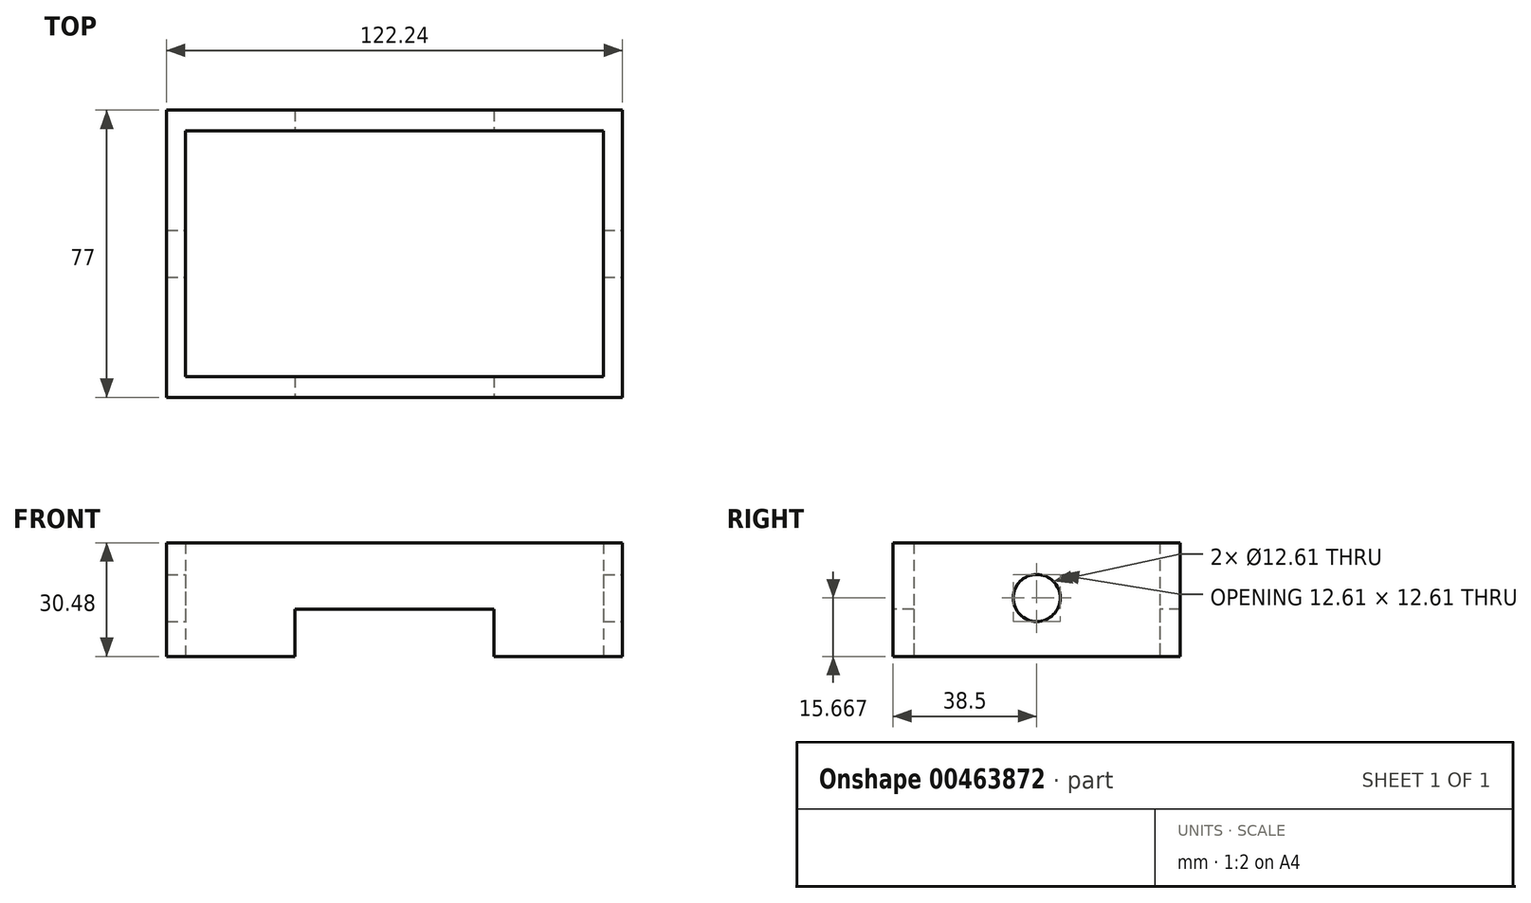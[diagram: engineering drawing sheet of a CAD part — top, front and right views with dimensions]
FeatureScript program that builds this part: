
annotation { "Feature Type Name" : "Feature", "Feature Type Description" : "" }
export const myFeature = defineFeature(function(context is Context, id is Id, definition is map)
    precondition{}
    {
        {
            var Q0;
            Q0=qCreatedBy(makeId("Top.planeOp"),FACE);
            var sketch = newSketch(context, id + "F0", { "sketchPlane" : qUnion([Q0])});
            skLineSegment(sketch, "E0.bottom", {"start": v(-61.12, 38.5) * mm, "end": v(61.12, 38.5) * mm});
            skLineSegment(sketch, "E0.top", {"start": v(-61.12, -38.5) * mm, "end": v(61.12, -38.5) * mm});
            skLineSegment(sketch, "E0.left", {"start": v(-61.12, 38.5) * mm, "end": v(-61.12, -38.5) * mm});
            skLineSegment(sketch, "E0.right", {"start": v(61.12, 38.5) * mm, "end": v(61.12, -38.5) * mm});
            skPoint(sketch, "E0.middle", {"position": v(0, 0) * mm});
            skSolve(sketch);
        }
        {
            var Q0;
            Q0=makeQuery(id+"F0.imprint","IMPRINT",FACE,{"disambiguationData":[TD([[makeQuery(id+"F0.imprint","IMPRINT",EDGE,{"derivedFrom":sQuery(id+"F0.wireOp",EDGE,"E0.bottom")}),-1.0]])]});
            extrude(context, id + "F1", {"entities" : qUnion([Q0]), "depth" : 30.48 * mm});
        }
        {
            var Q0;
            Q0=makeQuery(id+"F1.opExtrude","CAP_FACE",FACE,{"disambiguationData":[OSD([sQuery(id+"F0.wireOp",EDGE,"E0.bottom"),sQuery(id+"F0.wireOp",EDGE,"E0.top"),sQuery(id+"F0.wireOp",EDGE,"E0.left"),sQuery(id+"F0.wireOp",EDGE,"E0.right")])],"isStart":true});
            var sketch = newSketch(context, id + "F2", { "sketchPlane" : qUnion([Q0])});
            skLineSegment(sketch, "E1.bottom", {"start": v(56.02, 32.93) * mm, "end": v(-56.02, 32.93) * mm});
            skLineSegment(sketch, "E1.top", {"start": v(56.02, -32.93) * mm, "end": v(-56.02, -32.93) * mm});
            skLineSegment(sketch, "E1.left", {"start": v(56.02, 32.93) * mm, "end": v(56.02, -32.93) * mm});
            skLineSegment(sketch, "E1.right", {"start": v(-56.02, 32.93) * mm, "end": v(-56.02, -32.93) * mm});
            skPoint(sketch, "E1.middle", {"position": v(0, 0) * mm});
            skSolve(sketch);
        }
        {
            var Q0;
            Q0=makeQuery(id+"F2.imprint","IMPRINT",FACE,{"disambiguationData":[TD([[makeQuery(id+"F2.imprint","IMPRINT",EDGE,{"derivedFrom":sQuery(id+"F2.wireOp",EDGE,"E1.bottom")}),1.0]])]});
            extrude(context, id + "F3", {"entities" : qUnion([Q0]), "operationType" : NewBodyOperationType.REMOVE, "oppositeDirection" : true, "depth" : 120.65 * mm});
        }
        {
            var Q0;
            Q0=makeQuery(id+"F1.opExtrude","SWEPT_FACE",FACE,{"disambiguationData":[OSD([sQuery(id+"F0.wireOp",EDGE,"E0.right")])]});
            var sketch = newSketch(context, id + "F4", { "sketchPlane" : qUnion([Q0])});
            skCircle(sketch, "E2", {"center": v(0, 15.67) * mm, "radius": 6.3 * mm});
            skSolve(sketch);
        }
        {
            var Q0;
            Q0=makeQuery(id+"F4.imprint","IMPRINT",FACE,{"disambiguationData":[TD([[makeQuery(id+"F4.imprint","IMPRINT",EDGE,{"derivedFrom":sQuery(id+"F4.wireOp",EDGE,"E2")}),1.0]])]});
            extrude(context, id + "F5", {"entities" : qUnion([Q0]), "operationType" : NewBodyOperationType.REMOVE, "oppositeDirection" : true, "depth" : 227.33 * mm});
        }
        {
            var Q0;
            Q0=makeQuery(id+"F1.opExtrude","SWEPT_FACE",FACE,{"disambiguationData":[OSD([sQuery(id+"F0.wireOp",EDGE,"E0.top")])]});
            var sketch = newSketch(context, id + "F6", { "sketchPlane" : qUnion([Q0])});
            skLineSegment(sketch, "E3.bottom", {"start": v(-26.66, 12.67) * mm, "end": v(26.66, 12.67) * mm});
            skLineSegment(sketch, "E3.top", {"start": v(-26.66, -12.67) * mm, "end": v(26.66, -12.67) * mm});
            skLineSegment(sketch, "E3.left", {"start": v(-26.66, 12.67) * mm, "end": v(-26.66, -12.67) * mm});
            skLineSegment(sketch, "E3.right", {"start": v(26.66, 12.67) * mm, "end": v(26.66, -12.67) * mm});
            skPoint(sketch, "E3.middle", {"position": v(0, 0) * mm});
            skSolve(sketch);
        }
        {
            var Q0;
            {var subQ0=sQuery(id+"F6.wireOp",EDGE,"E3.bottom");Q0=makeQuery(id+"F6.imprint","IMPRINT",FACE,{"disambiguationData":[TD([[makeQuery(id+"F6.imprint","IMPRINT",EDGE,{"derivedFrom":subQ0}),-1.0]])]});}
            extrude(context, id + "F7", {"entities" : qUnion([Q0]), "operationType" : NewBodyOperationType.REMOVE, "oppositeDirection" : true, "depth" : 179.58 * mm});
        }
    });
